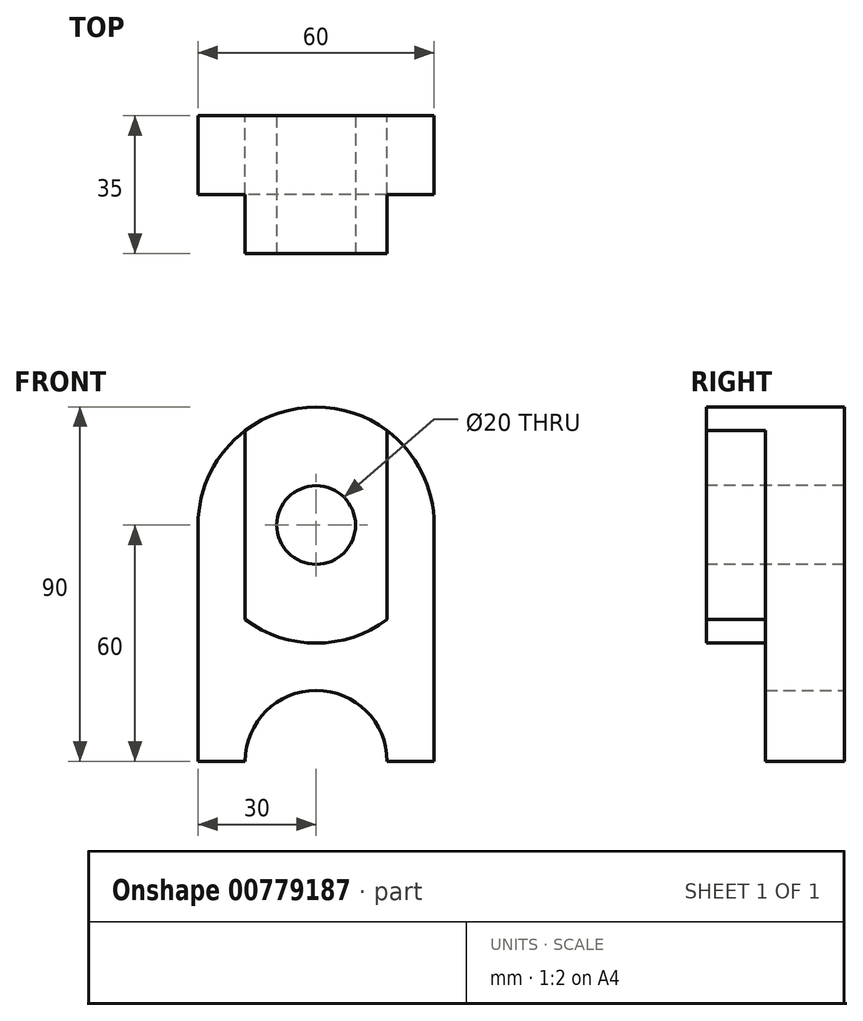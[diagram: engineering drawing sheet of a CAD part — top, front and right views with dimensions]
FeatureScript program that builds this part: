
annotation { "Feature Type Name" : "Feature", "Feature Type Description" : "" }
export const myFeature = defineFeature(function(context is Context, id is Id, definition is map)
    precondition{}
    {
        {
            var Q0;
            Q0=qCreatedBy(makeId("Front.planeOp"),FACE);
            var sketch = newSketch(context, id + "F0", { "sketchPlane" : qUnion([Q0])});
            skLineSegment(sketch, "E0.bottom", {"start": v(30, -30) * mm, "end": v(18, -30) * mm});
            skLineSegment(sketch, "E0.left", {"start": v(30, -30) * mm, "end": v(30, 30) * mm});
            skLineSegment(sketch, "E0.right", {"start": v(-30, -30) * mm, "end": v(-30, 30) * mm});
            skPoint(sketch, "E0.middle", {"position": v(0, 0) * mm});
            skArc(sketch, "E1", {"start": v(30, 30) * mm, "mid": v(0, 60) * mm, "end": v(-30, 30) * mm});
            skPoint(sketch, "E2", {"position": v(-18, -30) * mm});
            skPoint(sketch, "E3", {"position": v(18, -30) * mm});
            skPoint(sketch, "E4", {"position": v(30, -30) * mm});
            skArc(sketch, "E5", {"start": v(18, -30) * mm, "mid": v(0, -12) * mm, "end": v(-18, -30) * mm});
            skLineSegment(sketch, "E6.trimOffspring", {"start": v(-18, -30) * mm, "end": v(-30, -30) * mm});
            skSolve(sketch);
        }
        {
            var Q0;
            Q0=makeQuery(id+"F0.imprint","IMPRINT",FACE,{"disambiguationData":[TD([[makeQuery(id+"F0.imprint","IMPRINT",EDGE,{"derivedFrom":sQuery(id+"F0.wireOp",EDGE,"E0.bottom")}),-1.0]])]});
            extrude(context, id + "F1", {"entities" : qUnion([Q0]), "depth" : 20 * mm, "offsetDistance" : 25 * mm});
        }
        {
            var Q0;
            Q0=makeQuery(id+"F1.opExtrude","CAP_FACE",FACE,{"disambiguationData":[OSD([sQuery(id+"F0.wireOp",EDGE,"E0.bottom"),sQuery(id+"F0.wireOp",EDGE,"E0.left"),sQuery(id+"F0.wireOp",EDGE,"E0.right"),sQuery(id+"F0.wireOp",EDGE,"E1"),sQuery(id+"F0.wireOp",EDGE,"E5"),sQuery(id+"F0.wireOp",EDGE,"E6.trimOffspring")])],"isStart":false});
            var sketch = newSketch(context, id + "F2", { "sketchPlane" : qUnion([Q0])});
            skArc(sketch, "E7", {"start": v(-18, 6) * mm, "mid": v(0, 0) * mm, "end": v(18, 6) * mm});
            skPoint(sketch, "E8", {"position": v(-18, 30) * mm});
            skPoint(sketch, "E9", {"position": v(18, 30) * mm});
            skLineSegment(sketch, "E10", {"start": v(-18, 30) * mm, "end": v(-18, 6) * mm});
            skLineSegment(sketch, "E11", {"start": v(-18, 6) * mm, "end": v(-18, 30) * mm});
            skLineSegment(sketch, "E12", {"start": v(-18, 54) * mm, "end": v(-18, 30) * mm});
            skLineSegment(sketch, "E13", {"start": v(18, 6) * mm, "end": v(18, 30) * mm});
            skLineSegment(sketch, "E14", {"start": v(18, 54) * mm, "end": v(18, 30) * mm});
            skPoint(sketch, "E15.orphan", {"position": v(30, 30) * mm});
            skPoint(sketch, "E16.orphan", {"position": v(-30, 30) * mm});
            skSolve(sketch);
        }
        {
            var Q0;
            Q0=makeQuery(id+"F2.imprint","IMPRINT",FACE,{"disambiguationData":[TD([[makeQuery(id+"F2.imprint","IMPRINT",EDGE,{"derivedFrom":sQuery(id+"F2.wireOp",EDGE,"E7")}),1.0]])]});
            extrude(context, id + "F3", {"entities" : qUnion([Q0]), "operationType" : NewBodyOperationType.ADD, "depth" : 15 * mm, "offsetDistance" : 25 * mm});
        }
        {
            var Q0;
            Q0=makeQuery(id+"F3.opExtrude","CAP_FACE",FACE,{"disambiguationData":[OSD([sQuery(id+"F0.wireOp",EDGE,"E1"),sQuery(id+"F2.wireOp",EDGE,"E7"),sQuery(id+"F2.wireOp",EDGE,"E11"),sQuery(id+"F2.wireOp",EDGE,"E12"),sQuery(id+"F2.wireOp",EDGE,"E13"),sQuery(id+"F2.wireOp",EDGE,"E14")])],"isStart":false});
            var sketch = newSketch(context, id + "F4", { "sketchPlane" : qUnion([Q0])});
            skCircle(sketch, "E17", {"center": v(0, 30) * mm, "radius": 10 * mm});
            skSolve(sketch);
        }
        {
            var Q0;
            Q0=makeQuery(id+"F4.imprint","IMPRINT",FACE,{"disambiguationData":[TD([[makeQuery(id+"F4.imprint","IMPRINT",EDGE,{"derivedFrom":sQuery(id+"F4.wireOp",EDGE,"E17")}),1.0]])]});
            extrude(context, id + "F5", {"entities" : qUnion([Q0]), "operationType" : NewBodyOperationType.REMOVE, "endBound" : BoundingType.THROUGH_ALL, "oppositeDirection" : true, "depth" : 25 * mm, "offsetDistance" : 25 * mm});
        }
    });
